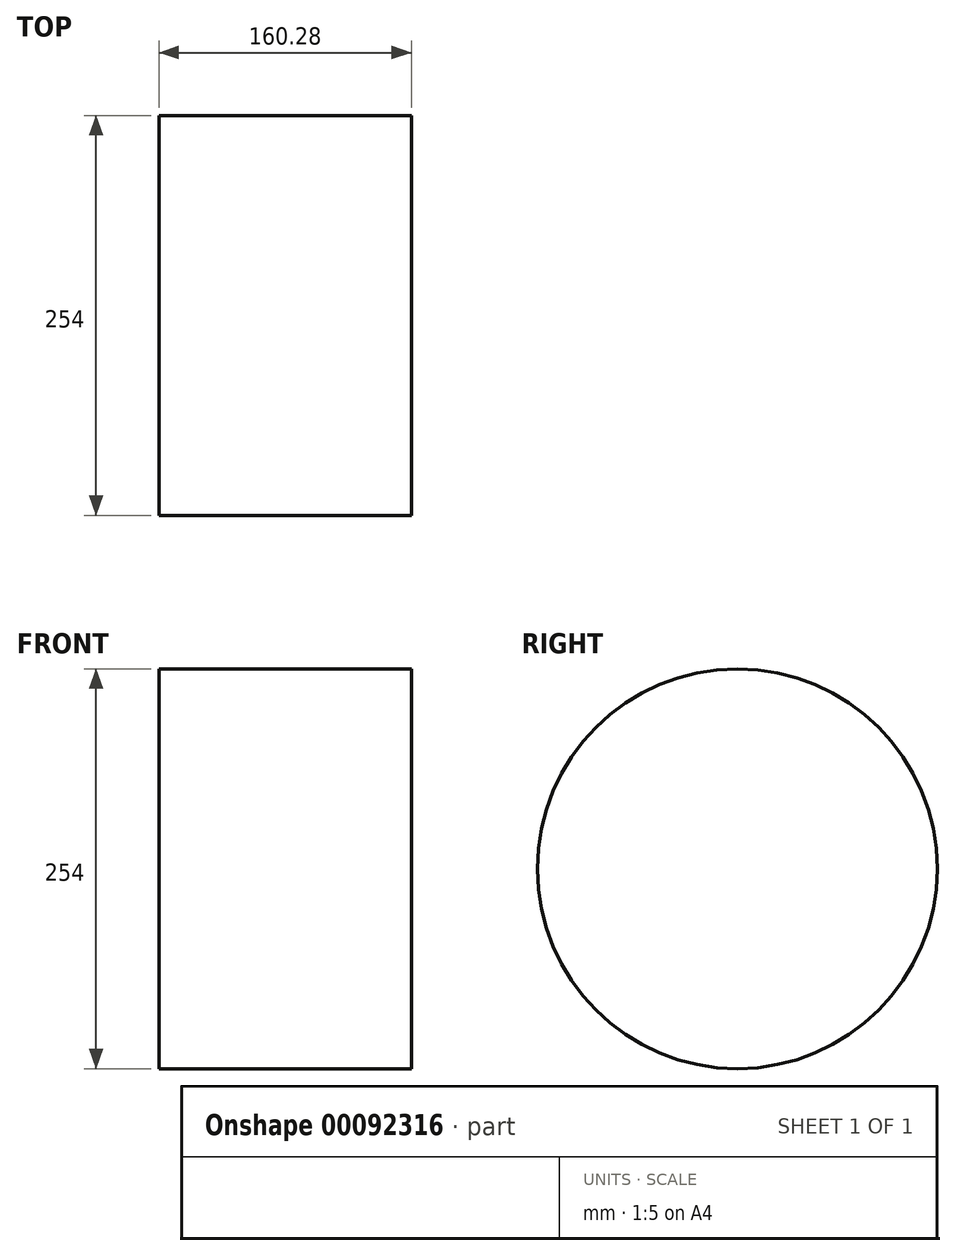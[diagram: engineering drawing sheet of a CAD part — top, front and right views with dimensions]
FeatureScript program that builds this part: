
annotation { "Feature Type Name" : "Feature", "Feature Type Description" : "" }
export const myFeature = defineFeature(function(context is Context, id is Id, definition is map)
    precondition{}
    {
        {
            var Q0;
            Q0=qCreatedBy(makeId("Right.planeOp"),FACE);
            var sketch = newSketch(context, id + "F0", { "sketchPlane" : qUnion([Q0])});
            skCircle(sketch, "E0", {"center": v(0, 0) * mm, "radius": 127 * mm});
            skSolve(sketch);
        }
        {
            var Q0;
            Q0=makeQuery(id+"F0.imprint","IMPRINT",FACE,{"disambiguationData":[TD([[makeQuery(id+"F0.imprint","IMPRINT",EDGE,{"derivedFrom":sQuery(id+"F0.wireOp",EDGE,"E0")}),1.0]])]});
            var Q1;
            Q1 = qSketchRegion(id + "F0", true);
            extrude(context, id + "F1", {"entities" : qUnion([Q0, Q1]), "depth" : 160.28 * mm, "offsetDistance" : 25.4 * mm});
        }
    });
